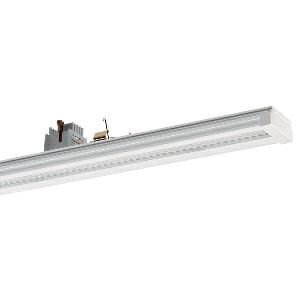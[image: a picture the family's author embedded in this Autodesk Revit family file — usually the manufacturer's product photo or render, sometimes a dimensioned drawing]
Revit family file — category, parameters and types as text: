
# Revit family: conveo_-_cvg_4500_840_w-l_ea_5_226848319-00804970_1ac8
name_source: partatom
category: Lighting Fixtures
units: mm (PartAtom-declared; Revit-internal decimal feet)

## family parameters
Cut with Voids When Loaded = No
Host = Face
Light Source = No
Part Type = Normal
Room Calculation Point = No
Round Connector Dimension = Use Diameter
Shared = No

## types (1)
- CONVEO - CVG 4500/840/W-L/EA/5 (1 x LED, 4450 lm, 4000K)
    Apparent Load = 24 VA
    Approval mark = CE
    CIE Flux Codes = 85 97 99 100 100
    Color Rendering = 80-89
    Color Temperature = 4000K
    Control Gear = Electronic ballast
    Default Elevation = 1800 mm
    Description = CVG 4500/840/W-L/EA/5|Continuous-row system|light source: LED|work equipment: Electronic ballast|connected load: 220-240 V, 50-60 Hz|Power consumption: approx. 24 W|luminous flux: 4450 lm|luminous efficacy: 185 lm/W|colour temperature: Cold white, ca. 4000 K|color rendering index (CRI): >= 80|chromaticity tolerance:  3 SDCM|System of protection: IP 54|class of protection: I|technology: Switchable|luminaire body|material: Aluminium|surface: Powder coatet|colour: White|lamp cover: Acrylic (PMMA), Satine|weight (net): approx. 1.9 kg|Fastening: Available separately|maximum ambient temperature: 50 ░C|glare control: Lens optics|Approval mark: VDE - ENEC|
    Frequency = 50 Hz
    Height = 70 mm
    Lamp = 1 x LED
    Lamp Light Flux = 4450 lm
    Lamp count = 1
    Length = 1500 mm
    Luminous efficacy = 185 lm/W
    Manufacturer = Waldmann
    ModVariant = No
    Model = 226848319-00804970
    Mounting Place = Ceiling
    Mounting Type = Pendant
    Number of Poles = 1
    OnlyDefault = Yes
    Power Factor = 1
    Product Name = CONVEO - CVG 4500/840/W-L/EA/5
    Product group = Continuous-row system (industry)
    ProductGroupID = 301
    Protection Class = Protection class I
    Protection Degree = IP 54
    RLX_Detail_Level = 1
    RlxData = <blob elided: 99825 chars, md5=22eceb6f>
    Socket = socket
    Standby Power = 0 W
    System Light Flux = 4450 lm
    System Power = 24 W
    Type Comments = Product without accessories
    Type Image = 226848319-00804970_1l5.jpg
    URL = http://relux.com
    VarID = ---
    Voltage = 230 V
    Voltage Range = 220-240 V
    Weight = 0.00 kg
    Width = 64 mm

## geometry (parser evidence)
native form markers: Blend x4, Sweep x10
no freeform markers — native parametric forms only
